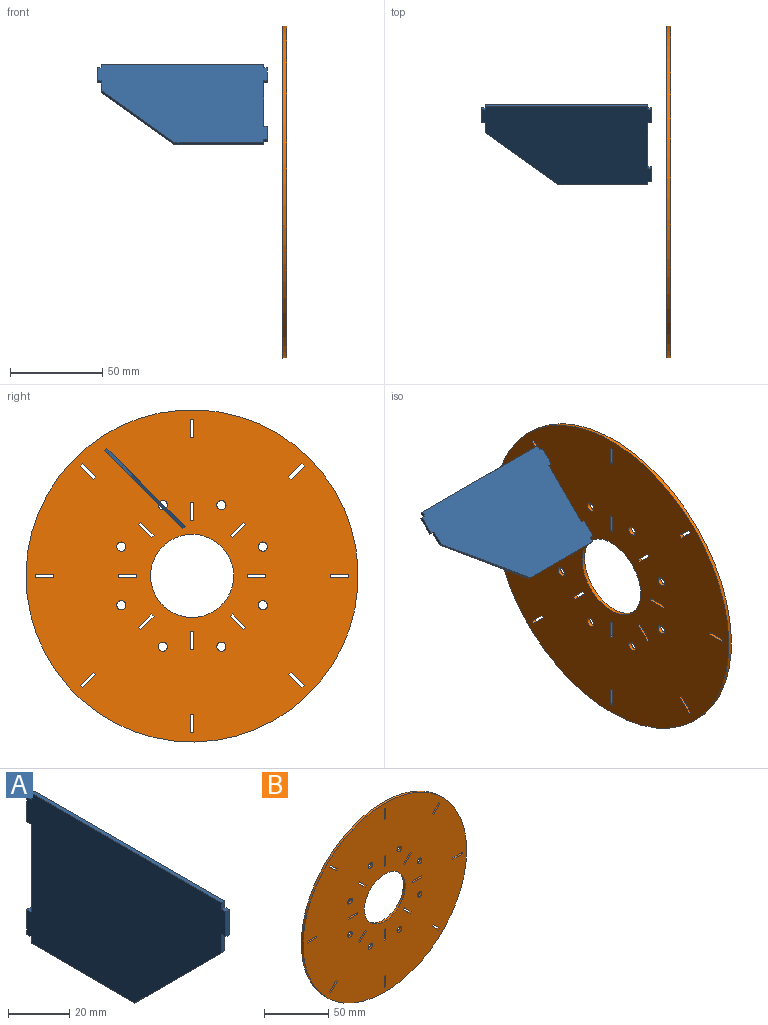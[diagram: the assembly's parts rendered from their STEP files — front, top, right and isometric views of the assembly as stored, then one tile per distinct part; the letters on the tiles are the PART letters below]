
ASSEMBLY  parts=2 mates=3
PART A: 19 faces, bbox 1.6x92x60 mm
  f0: plane 2x1.6mm, normal (0,0,-1), area 3.2mm2, adj f1,f15,f16,f17
  f1: plane 7.5x1.6mm, normal (0,-1,0), area 12mm2, adj f0,f16,f17,f18
  f2: plane 48x1.6mm, normal (0,0,-1), area 76.8mm2, adj f3,f16,f17,f18
  f3: plane 2.55x1.6mm, normal (0,1,0), area 4.1mm2, adj f2,f4,f16,f17
  f4: plane 2x1.6mm, normal (0,0,-1), area 3.2mm2, adj f3,f5,f16,f17
  f5: plane 9.9x1.6mm, normal (0,1,0), area 15.8mm2, adj f4,f6,f16,f17
  f6: plane 2x1.6mm, normal (0,0,1), area 3.2mm2, adj f5,f7,f16,f17
  f7: plane 35.1x1.6mm, normal (0,1,0), area 56.2mm2, adj f6,f8,f16,f17
  f8: plane 2x1.6mm, normal (0,0,-1), area 3.2mm2, adj f7,f9,f16,f17
  f9: plane 9.9x1.6mm, normal (0,1,0), area 15.8mm2, adj f8,f10,f16,f17
  f10: plane 2x1.6mm, normal (0,0,1), area 3.2mm2, adj f9,f11,f16,f17
  f11: plane 2.55x1.6mm, normal (0,1,0), area 4.1mm2, adj f10,f12,f16,f17
  f12: plane 88x1.6mm, normal (0,0,1), area 140.8mm2, adj f11,f13,f16,f17
  f13: plane 2.5x1.6mm, normal (0,-1,0), area 4mm2, adj f12,f14,f16,f17
  f14: plane 2x1.6mm, normal (0,0,1), area 3.2mm2, adj f13,f15,f16,f17
  f15: plane 10x1.6mm, normal (0,-1,0), area 16mm2, adj f0,f14,f16,f17
  f16: plane 92x60mm, normal (1,0,0), area 4539.6mm2, adj f0,f1,f2,f3,f4,f5,f6,f7
  f17: plane 92x60mm, normal (-1,0,0), area 4539.6mm2, adj f0,f1,f2,f3,f4,f5,f6,f7
  f18: plane 40x40mm, normal (0,-0.71,-0.71), area 90.5mm2, adj f1,f2,f16,f17
PART B: 76 faces, bbox 180x2x180 mm
  f0: plane 180x180mm, normal (0,-1,0), area 23435.4mm2, adj f2,f3,f4,f5,f6,f7,f8,f9
  f1: plane 180x180mm, normal (0,1,0), area 23435.4mm2, adj f2,f3,f4,f5,f6,f7,f8,f9
  f2: cylinder r=22.5mm len=45mm, axis (0,1,0), area 282.7mm2, adj f0,f1
  f3: cylinder r=90mm len=180mm, axis (0,1,0), area 1131mm2, adj f0,f1
  f4: cylinder r=2.5mm len=5mm, axis (0,-1,0), area 31.4mm2, adj f0,f1
  f5: cylinder r=2.5mm len=5mm, axis (0,-1,0), area 31.4mm2, adj f0,f1
  f6: cylinder r=2.5mm len=5mm, axis (0,-1,0), area 31.4mm2, adj f0,f1
  f7: cylinder r=2.5mm len=5mm, axis (0,-1,0), area 31.4mm2, adj f0,f1
  f8: cylinder r=2.5mm len=5mm, axis (0,-1,0), area 31.4mm2, adj f0,f1
  f9: cylinder r=2.5mm len=5mm, axis (0,-1,0), area 31.4mm2, adj f0,f1
  f10: cylinder r=2.5mm len=5mm, axis (0,-1,0), area 31.4mm2, adj f0,f1
  f11: cylinder r=2.5mm len=5mm, axis (0,-1,0), area 31.4mm2, adj f0,f1
  f12: plane 2x1.65mm, normal (0,0,-1), area 3.3mm2, adj f0,f1,f13,f14
  f13: plane 10x2mm, normal (-1,0,0), area 20mm2, adj f0,f1,f12,f15
  f14: plane 10x2mm, normal (1,0,0), area 20mm2, adj f0,f1,f12,f15
  f15: plane 2x1.65mm, normal (0,0,1), area 3.3mm2, adj f0,f1,f13,f14
  f16: plane 2x1.17mm, normal (-0.71,0,-0.71), area 3.3mm2, adj f0,f1,f17,f18
  f17: plane 7.07x7.07mm, normal (-0.71,0,0.71), area 20mm2, adj f0,f1,f16,f19
  f18: plane 7.07x7.07mm, normal (0.71,0,-0.71), area 20mm2, adj f0,f1,f16,f19
  f19: plane 2x1.17mm, normal (0.71,0,0.71), area 3.3mm2, adj f0,f1,f17,f18
  f20: plane 2x1.17mm, normal (-0.71,0,-0.71), area 3.3mm2, adj f0,f1,f21,f22
  f21: plane 7.07x7.07mm, normal (-0.71,0,0.71), area 20mm2, adj f0,f1,f20,f23
  f22: plane 7.07x7.07mm, normal (0.71,0,-0.71), area 20mm2, adj f0,f1,f20,f23
  f23: plane 2x1.17mm, normal (0.71,0,0.71), area 3.3mm2, adj f0,f1,f21,f22
  f24: plane 2x1.65mm, normal (-1,0,0), area 3.3mm2, adj f0,f1,f25,f26
  f25: plane 10x2mm, normal (0,0,1), area 20mm2, adj f0,f1,f24,f27
  f26: plane 10x2mm, normal (0,0,-1), area 20mm2, adj f0,f1,f24,f27
  f27: plane 2x1.65mm, normal (1,0,0), area 3.3mm2, adj f0,f1,f25,f26
  f28: plane 2x1.65mm, normal (-1,0,0), area 3.3mm2, adj f0,f1,f29,f30
  f29: plane 10x2mm, normal (0,0,1), area 20mm2, adj f0,f1,f28,f31
  f30: plane 10x2mm, normal (0,0,-1), area 20mm2, adj f0,f1,f28,f31
  f31: plane 2x1.65mm, normal (1,0,0), area 3.3mm2, adj f0,f1,f29,f30
  f32: plane 2x1.17mm, normal (-0.71,0,0.71), area 3.3mm2, adj f0,f1,f33,f34
  f33: plane 7.07x7.07mm, normal (0.71,0,0.71), area 20mm2, adj f0,f1,f32,f35
  f34: plane 7.07x7.07mm, normal (-0.71,0,-0.71), area 20mm2, adj f0,f1,f32,f35
  f35: plane 2x1.17mm, normal (0.71,0,-0.71), area 3.3mm2, adj f0,f1,f33,f34
  f36: plane 2x1.17mm, normal (-0.71,0,0.71), area 3.3mm2, adj f0,f1,f37,f38
  f37: plane 7.07x7.07mm, normal (0.71,0,0.71), area 20mm2, adj f0,f1,f36,f39
  f38: plane 7.07x7.07mm, normal (-0.71,0,-0.71), area 20mm2, adj f0,f1,f36,f39
  f39: plane 2x1.17mm, normal (0.71,0,-0.71), area 3.3mm2, adj f0,f1,f37,f38
  f40: plane 2x1.65mm, normal (0,0,-1), area 3.3mm2, adj f0,f1,f41,f42
  f41: plane 10x2mm, normal (1,0,0), area 20mm2, adj f0,f1,f40,f43
  f42: plane 10x2mm, normal (-1,0,0), area 20mm2, adj f0,f1,f40,f43
  f43: plane 2x1.65mm, normal (0,0,1), area 3.3mm2, adj f0,f1,f41,f42
  f44: plane 2x1.17mm, normal (0.71,0,0.71), area 3.3mm2, adj f0,f1,f45,f46
  f45: plane 7.07x7.07mm, normal (0.71,0,-0.71), area 20mm2, adj f0,f1,f44,f47
  f46: plane 7.07x7.07mm, normal (-0.71,0,0.71), area 20mm2, adj f0,f1,f44,f47
  f47: plane 2x1.17mm, normal (-0.71,0,-0.71), area 3.3mm2, adj f0,f1,f45,f46
  f48: plane 2x1.17mm, normal (0.71,0,0.71), area 3.3mm2, adj f0,f1,f49,f50
  f49: plane 7.07x7.07mm, normal (0.71,0,-0.71), area 20mm2, adj f0,f1,f48,f51
  f50: plane 7.07x7.07mm, normal (-0.71,0,0.71), area 20mm2, adj f0,f1,f48,f51
  f51: plane 2x1.17mm, normal (-0.71,0,-0.71), area 3.3mm2, adj f0,f1,f49,f50
  f52: plane 2x1.65mm, normal (1,0,0), area 3.3mm2, adj f0,f1,f53,f54
  f53: plane 10x2mm, normal (0,0,-1), area 20mm2, adj f0,f1,f52,f55
  f54: plane 10x2mm, normal (0,0,1), area 20mm2, adj f0,f1,f52,f55
  f55: plane 2x1.65mm, normal (-1,0,0), area 3.3mm2, adj f0,f1,f53,f54
  f56: plane 2x1.65mm, normal (1,0,0), area 3.3mm2, adj f0,f1,f57,f58
  f57: plane 10x2mm, normal (0,0,-1), area 20mm2, adj f0,f1,f56,f59
  f58: plane 10x2mm, normal (0,0,1), area 20mm2, adj f0,f1,f56,f59
  f59: plane 2x1.65mm, normal (-1,0,0), area 3.3mm2, adj f0,f1,f57,f58
  f60: plane 2x1.17mm, normal (0.71,0,-0.71), area 3.3mm2, adj f0,f1,f61,f62
  f61: plane 7.07x7.07mm, normal (-0.71,0,-0.71), area 20mm2, adj f0,f1,f60,f63
  f62: plane 7.07x7.07mm, normal (0.71,0,0.71), area 20mm2, adj f0,f1,f60,f63
  f63: plane 2x1.17mm, normal (-0.71,0,0.71), area 3.3mm2, adj f0,f1,f61,f62
  f64: plane 2x1.17mm, normal (0.71,0,-0.71), area 3.3mm2, adj f0,f1,f65,f66
  f65: plane 7.07x7.07mm, normal (-0.71,0,-0.71), area 20mm2, adj f0,f1,f64,f67
  f66: plane 7.07x7.07mm, normal (0.71,0,0.71), area 20mm2, adj f0,f1,f64,f67
  f67: plane 2x1.17mm, normal (-0.71,0,0.71), area 3.3mm2, adj f0,f1,f65,f66
  f68: plane 2x1.65mm, normal (0,0,-1), area 3.3mm2, adj f0,f1,f69,f70
  f69: plane 10x2mm, normal (-1,0,0), area 20mm2, adj f0,f1,f68,f71
  f70: plane 10x2mm, normal (1,0,0), area 20mm2, adj f0,f1,f68,f71
  f71: plane 2x1.65mm, normal (0,0,1), area 3.3mm2, adj f0,f1,f69,f70
  f72: plane 2x1.65mm, normal (0,0,1), area 3.3mm2, adj f0,f1,f73,f74
  f73: plane 10x2mm, normal (1,0,0), area 20mm2, adj f0,f1,f72,f75
  f74: plane 10x2mm, normal (-1,0,0), area 20mm2, adj f0,f1,f72,f75
  f75: plane 2x1.65mm, normal (0,0,-1), area 3.3mm2, adj f0,f1,f73,f74
PLACE A rot(axis=(-0.36,-0.36,-0.86),98.4deg) t=(-81.38,-80.43,102.01)mm
PLACE B rot(axis=(-0.36,-0.36,-0.86),98.4deg) t=(-70.93,-65.35,95.37)mm
MATE parallel B.f72 <-> A.f8  axis (0,0.71,0.71) through (-71.93,-12.31,148.41)mm
MATE parallel B.f75 <-> A.f10  axis (0,-0.71,-0.71) through (-71.93,-5.24,155.48)mm
MATE parallel A.f16 <-> B.f74  axis (0,-0.71,0.71) through (-121.78,-38.19,145.38)mm
